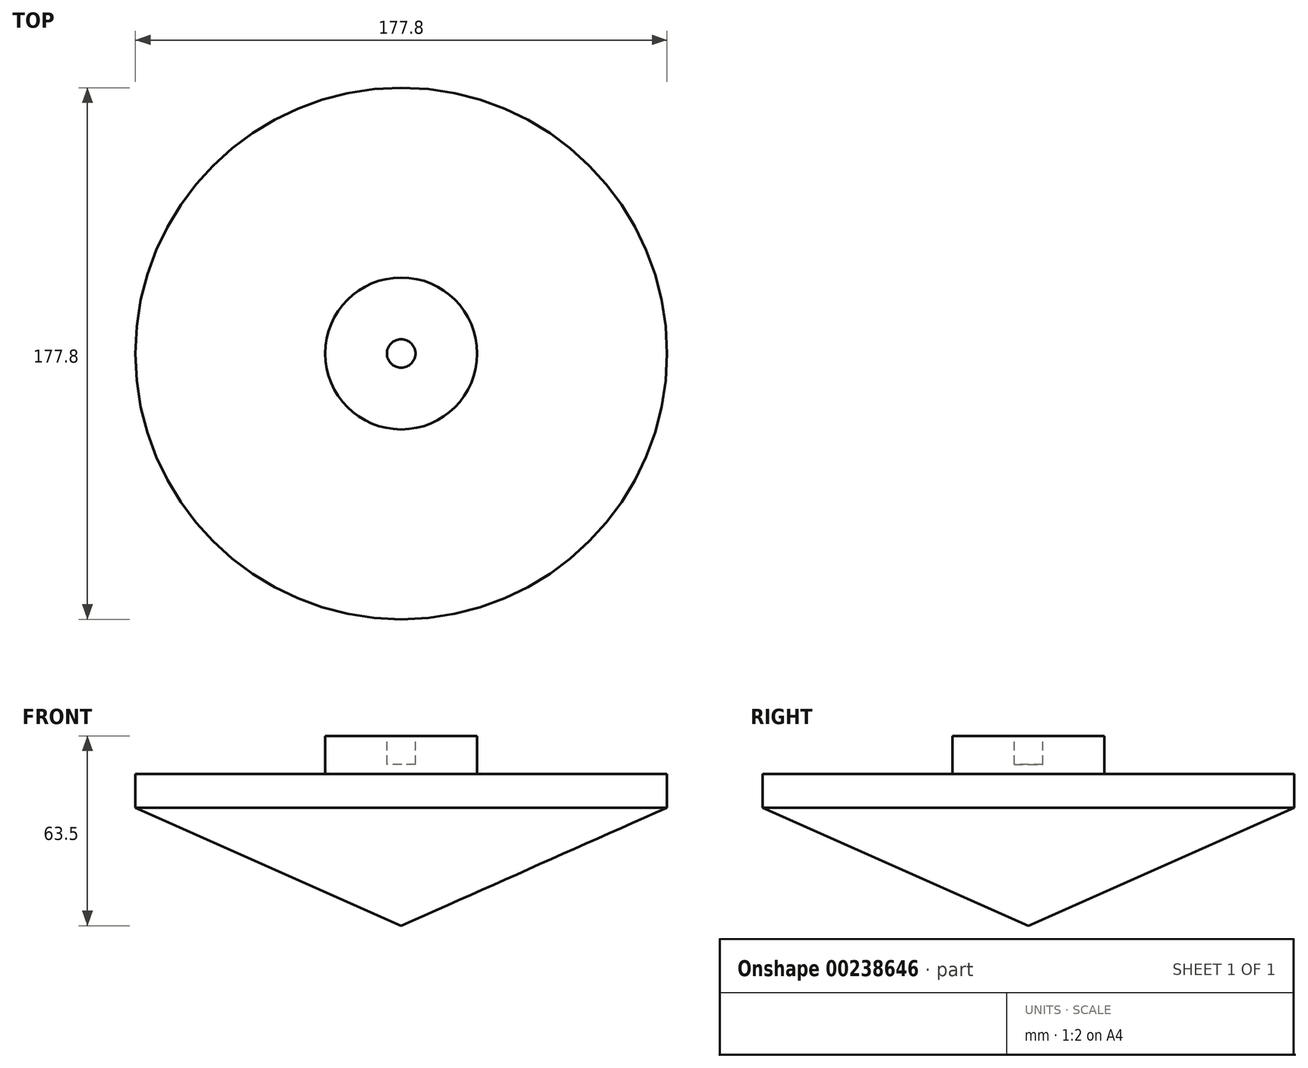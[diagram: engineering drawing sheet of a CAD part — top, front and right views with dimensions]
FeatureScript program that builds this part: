
annotation { "Feature Type Name" : "Feature", "Feature Type Description" : "" }
export const myFeature = defineFeature(function(context is Context, id is Id, definition is map)
    precondition{}
    {
        {
            var Q0;
            Q0=qCreatedBy(makeId("Front.planeOp"),FACE);
            var sketch = newSketch(context, id + "F0", { "sketchPlane" : qUnion([Q0])});
            skLineSegment(sketch, "E0", {"start": v(0, 0) * mm, "end": v(88.9, 39.46) * mm});
            skLineSegment(sketch, "E1", {"start": v(88.9, 39.46) * mm, "end": v(88.9, 50.8) * mm});
            skLineSegment(sketch, "E2", {"start": v(88.9, 50.8) * mm, "end": v(25.4, 50.8) * mm});
            skLineSegment(sketch, "E3", {"start": v(25.4, 50.8) * mm, "end": v(25.4, 63.5) * mm});
            skLineSegment(sketch, "E4", {"start": v(25.4, 63.5) * mm, "end": v(0, 63.5) * mm});
            skLineSegment(sketch, "E5", {"start": v(0, 63.5) * mm, "end": v(0, 0) * mm});
            skSolve(sketch);
        }
        {
            var Q0;
            Q0 = qSketchRegion(id + "F0", true);
            var Q1;
            Q1=sQuery(id+"F0.wireOp",EDGE,"E5");
            revolve(context, id + "F1", {"entities" : qUnion([Q0]), "axis" : qUnion([Q1]), "revolveType" : RevolveType.FULL});
        }
        {
            var Q0;
            Q0=makeQuery(id+"F1.opRevolve","SWEPT_FACE",FACE,{"disambiguationData":[OSD([sQuery(id+"F0.wireOp",EDGE,"E4")])]});
            var sketch = newSketch(context, id + "F2", { "sketchPlane" : qUnion([Q0])});
            skCircle(sketch, "E6", {"center": v(0, 0) * mm, "radius": 4.76 * mm});
            skSolve(sketch);
        }
        {
            var Q0;
            Q0 = qSketchRegion(id + "F2", true);
            extrude(context, id + "F3", {"entities" : qUnion([Q0]), "operationType" : NewBodyOperationType.REMOVE, "oppositeDirection" : true, "depth" : 9.52 * mm});
        }
        {
            var Q0;
            Q0=qCreatedBy(makeId("Top.planeOp"),FACE);
            var sketch = newSketch(context, id + "F4", { "sketchPlane" : qUnion([Q0])});
            skCircle(sketch, "E7", {"center": v(0, 0) * mm, "radius": 1.59 * mm});
            skSolve(sketch);
        }
        {
            var Q0;
            Q0=sQuery(id+"F4.wireOp",EDGE,"E7");
            extrude(context, id + "F5", {"bodyType" : ToolBodyType.SURFACE, "operationType" : NewBodyOperationType.REMOVE, "surfaceEntities" : qUnion([Q0]), "depth" : 22.22 * mm});
        }
    });
